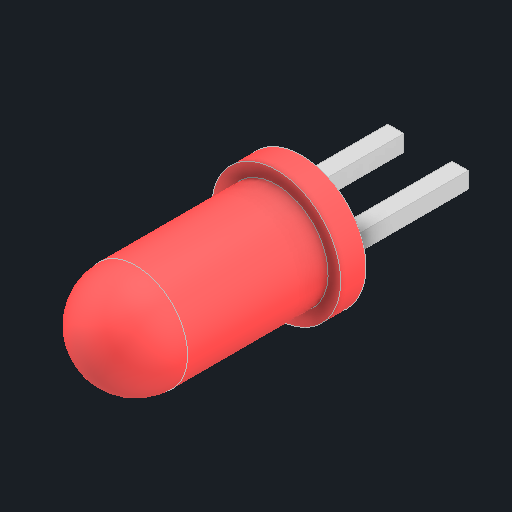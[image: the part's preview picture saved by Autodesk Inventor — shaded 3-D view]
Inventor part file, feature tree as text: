
AUTODESK INVENTOR PART (.ipt)
format: ipt  version: 2022 (Build 260153000, 153)  size: 131,072 bytes
history: imported  units: in
note: dims shown in document units (in); Inventor stores cm internally (conversion verified against a paired STEP export)
features: imported_body x1
ambient origin geometry x8: Origin, YZ Plane, XZ Plane, XY Plane, X Axis, Y Axis, Z Axis, Center Point
bodies: Solid1 (imported_parasolid), Body1 (imported_parasolid)
feature tree (1):
  imported_body  NMx_Import_Brep_tag  [imported B-rep: ~15 faces, bbox_mm=[3.18, 2.87, 11.55]]
